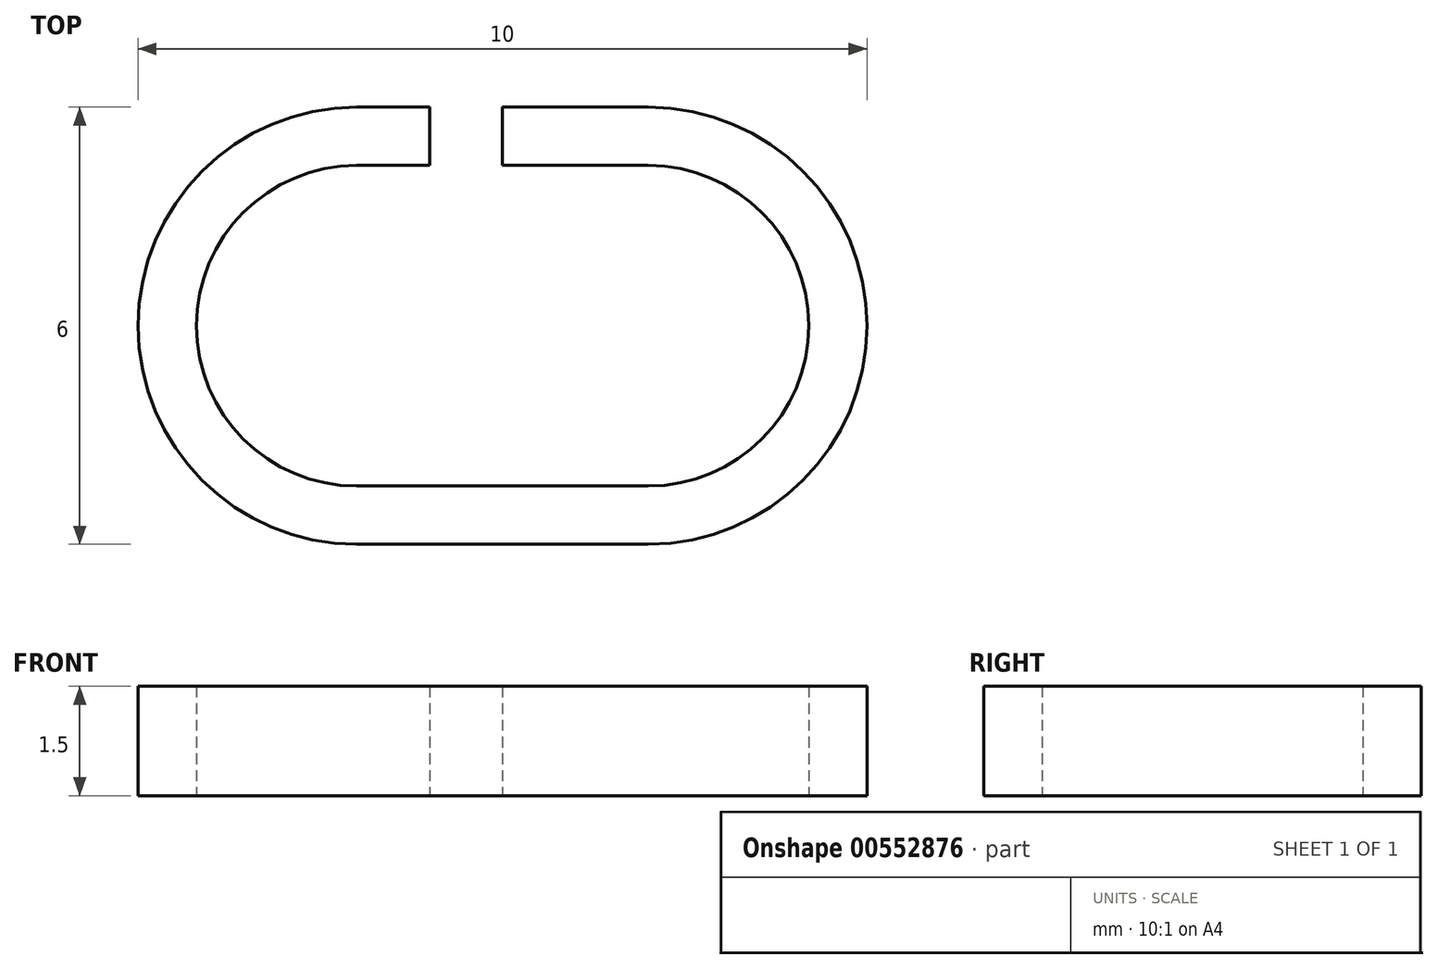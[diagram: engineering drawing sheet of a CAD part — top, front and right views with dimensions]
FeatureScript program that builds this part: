
annotation { "Feature Type Name" : "Feature", "Feature Type Description" : "" }
export const myFeature = defineFeature(function(context is Context, id is Id, definition is map)
    precondition{}
    {
        {
            var Q0;
            Q0=qCreatedBy(makeId("Top.planeOp"),FACE);
            var sketch = newSketch(context, id + "F0", { "sketchPlane" : qUnion([Q0])});
            skLineSegment(sketch, "E0.bottom", {"start": v(3, 0) * mm, "end": v(7, 0) * mm});
            skLineSegment(sketch, "E0.top", {"start": v(3, 6) * mm, "end": v(4, 6) * mm});
            skLineSegment(sketch, "E0.left", {"start": v(0, 3) * mm, "end": v(0, 3) * mm});
            skLineSegment(sketch, "E0.right", {"start": v(10, 3) * mm, "end": v(10, 3) * mm});
            skPoint(sketch, "E1.visualSharp", {"position": v(10, 6) * mm});
            skArc(sketch, "E1.filletArc", {"start": v(10, 3) * mm, "mid": v(9.12, 5.12) * mm, "end": v(7, 6) * mm});
            skPoint(sketch, "E2.visualSharp", {"position": v(0, 6) * mm});
            skArc(sketch, "E2.filletArc", {"start": v(3, 6) * mm, "mid": v(0.88, 5.12) * mm, "end": v(0, 3) * mm});
            skPoint(sketch, "E3.visualSharp", {"position": v(10, 0) * mm});
            skArc(sketch, "E3.filletArc", {"start": v(7, 0) * mm, "mid": v(9.12, 0.88) * mm, "end": v(10, 3) * mm});
            skPoint(sketch, "E4.visualSharp", {"position": v(0, 0) * mm});
            skArc(sketch, "E4.filletArc", {"start": v(0, 3) * mm, "mid": v(0.88, 0.88) * mm, "end": v(3, 0) * mm});
            skArc(sketch, "E5.0", {"start": v(3, 5.2) * mm, "mid": v(1.44, 4.56) * mm, "end": v(0.8, 3) * mm});
            skLineSegment(sketch, "E5.1", {"start": v(0.8, 3) * mm, "end": v(0.8, 3) * mm});
            skLineSegment(sketch, "E5.2", {"start": v(3, 5.2) * mm, "end": v(4, 5.2) * mm});
            skArc(sketch, "E5.3", {"start": v(0.8, 3) * mm, "mid": v(1.44, 1.44) * mm, "end": v(3, 0.8) * mm});
            skArc(sketch, "E5.4", {"start": v(9.2, 3) * mm, "mid": v(8.56, 4.56) * mm, "end": v(7, 5.2) * mm});
            skLineSegment(sketch, "E5.5", {"start": v(9.2, 3) * mm, "end": v(9.2, 3) * mm});
            skArc(sketch, "E5.6", {"start": v(7, 0.8) * mm, "mid": v(8.56, 1.44) * mm, "end": v(9.2, 3) * mm});
            skLineSegment(sketch, "E5.7", {"start": v(3, 0.8) * mm, "end": v(7, 0.8) * mm});
            skLineSegment(sketch, "E6.left", {"start": v(4, 6) * mm, "end": v(4, 5.2) * mm});
            skLineSegment(sketch, "E6.right", {"start": v(5, 6) * mm, "end": v(5, 5.2) * mm});
            skLineSegment(sketch, "E7.trimOffspring", {"start": v(5, 6) * mm, "end": v(7, 6) * mm});
            skLineSegment(sketch, "E8.trimOffspring", {"start": v(5, 5.2) * mm, "end": v(7, 5.2) * mm});
            skSolve(sketch);
        }
        {
            var Q0;
            Q0 = qSketchRegion(id + "F0", true);
            extrude(context, id + "F1", {"entities" : qUnion([Q0]), "depth" : 1.5 * mm, "offsetDistance" : 25 * mm});
        }
    });
